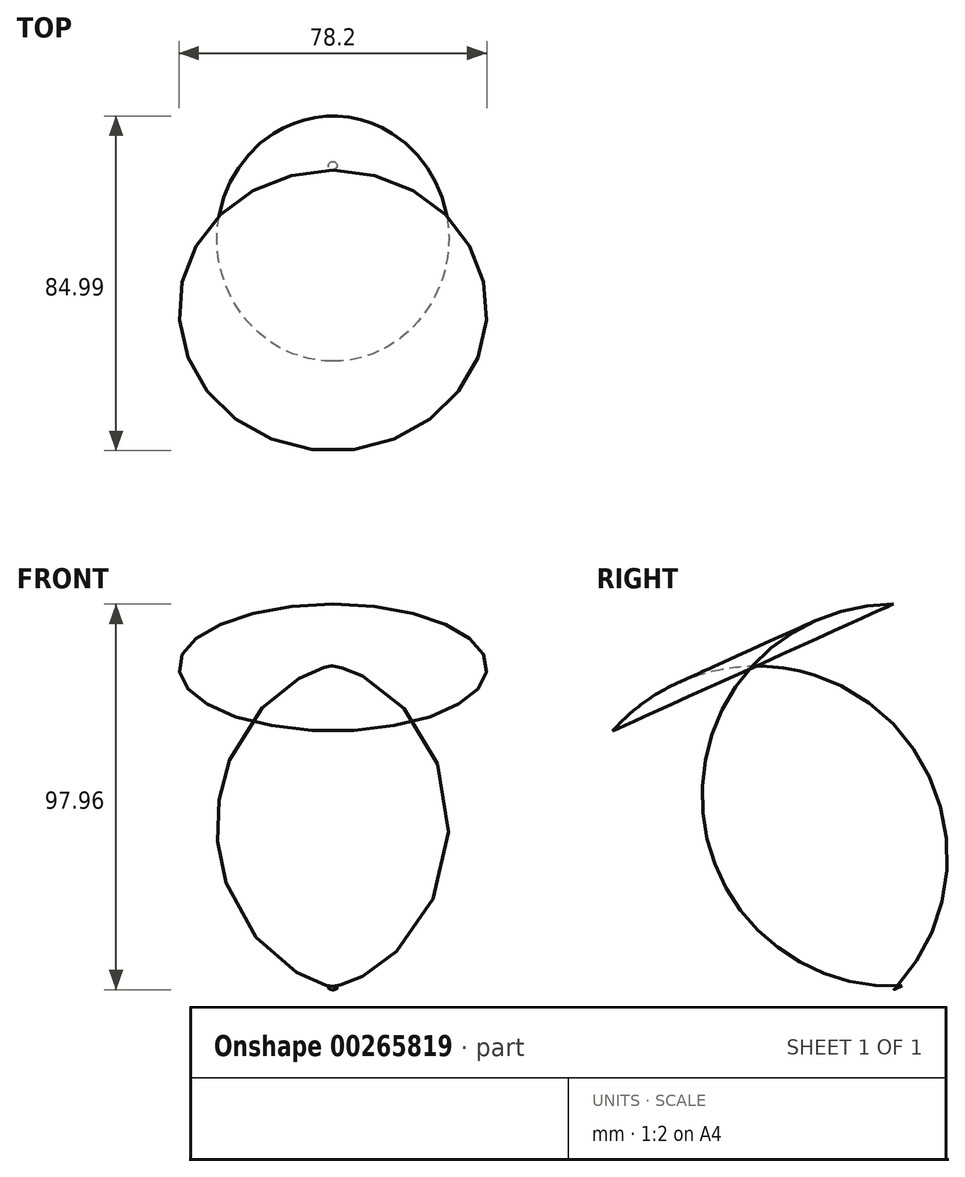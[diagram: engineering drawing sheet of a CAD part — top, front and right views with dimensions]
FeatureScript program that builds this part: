
annotation { "Feature Type Name" : "Feature", "Feature Type Description" : "" }
export const myFeature = defineFeature(function(context is Context, id is Id, definition is map)
    precondition{}
    {
        {
            var Q0;
            Q0=qCreatedBy(makeId("Right.planeOp"),FACE);
            var sketch = newSketch(context, id + "F0", { "sketchPlane" : qUnion([Q0])});
            skArc(sketch, "E0", {"start": v(0, 48.55) * mm, "mid": v(48.54, 1.1) * mm, "end": v(2.18, -48.5) * mm});
            skLineSegment(sketch, "E1", {"start": v(-42.26, 47.12) * mm, "end": v(11.7, -72.25) * mm});
            skSolve(sketch);
        }
        {
            var Q0;
            Q0=sQuery(id+"F0.wireOp",EDGE,"E0");
            var Q1;
            Q1=sQuery(id+"F0.wireOp",EDGE,"E1");
            revolve(context, id + "F1", {"bodyType" : ToolBodyType.SURFACE, "surfaceEntities" : qUnion([Q0]), "axis" : qUnion([Q1]), "revolveType" : RevolveType.FULL});
        }
    });
